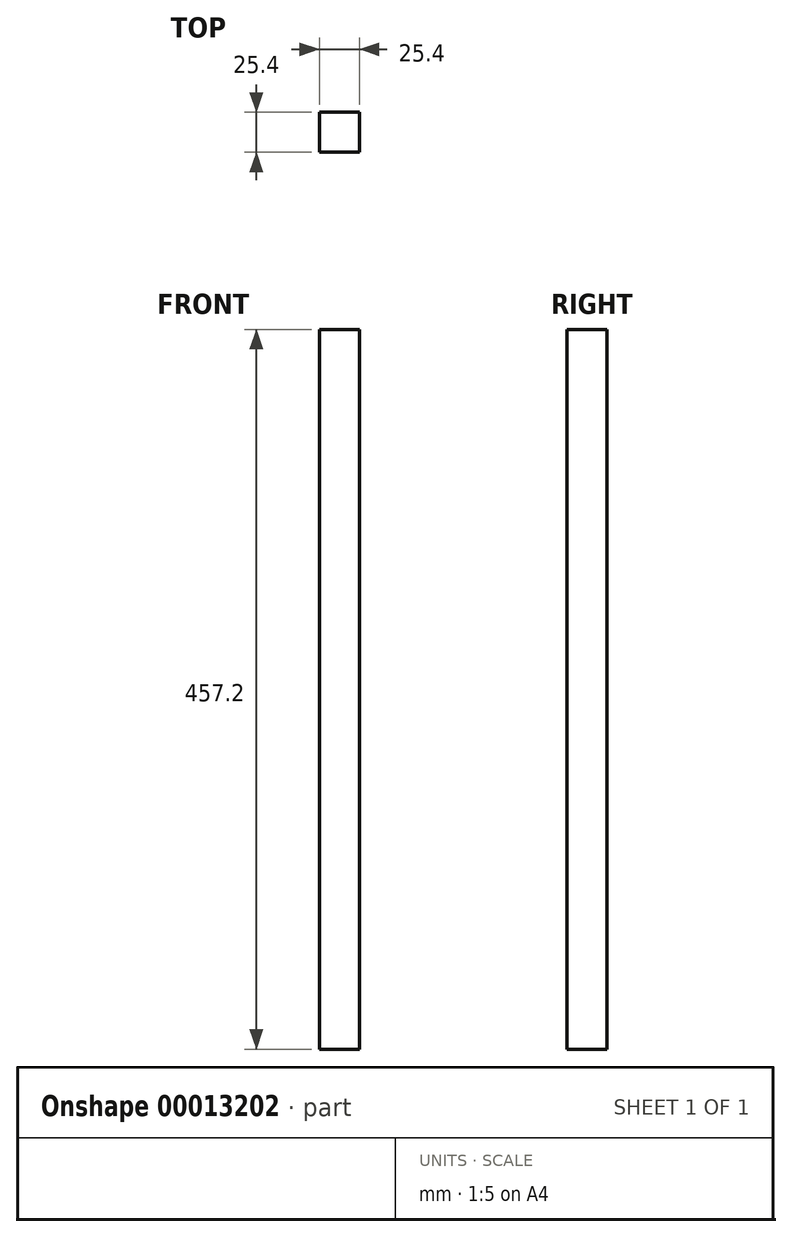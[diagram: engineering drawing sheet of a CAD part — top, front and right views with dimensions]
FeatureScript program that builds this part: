
annotation { "Feature Type Name" : "Feature", "Feature Type Description" : "" }
export const myFeature = defineFeature(function(context is Context, id is Id, definition is map)
    precondition{}
    {
        {
            var Q0;
            Q0=qCreatedBy(makeId("Top.planeOp"),FACE);
            var sketch = newSketch(context, id + "F0", { "sketchPlane" : qUnion([Q0])});
            skLineSegment(sketch, "E0.rect.bottom", {"start": v(12.7, -12.7) * mm, "end": v(-12.7, -12.7) * mm});
            skLineSegment(sketch, "E0.rect.top", {"start": v(12.7, 12.7) * mm, "end": v(-12.7, 12.7) * mm});
            skLineSegment(sketch, "E0.rect.left", {"start": v(12.7, -12.7) * mm, "end": v(12.7, 12.7) * mm});
            skLineSegment(sketch, "E0.rect.right", {"start": v(-12.7, -12.7) * mm, "end": v(-12.7, 12.7) * mm});
            skPoint(sketch, "E0.rect.middle", {"position": v(0, 0) * mm});
            skSolve(sketch);
        }
        {
            var Q0;
            Q0 = qSketchRegion(id + "F0", true);
            extrude(context, id + "F1", {"entities" : qUnion([Q0]), "depth" : 457.2 * mm});
        }
    });
